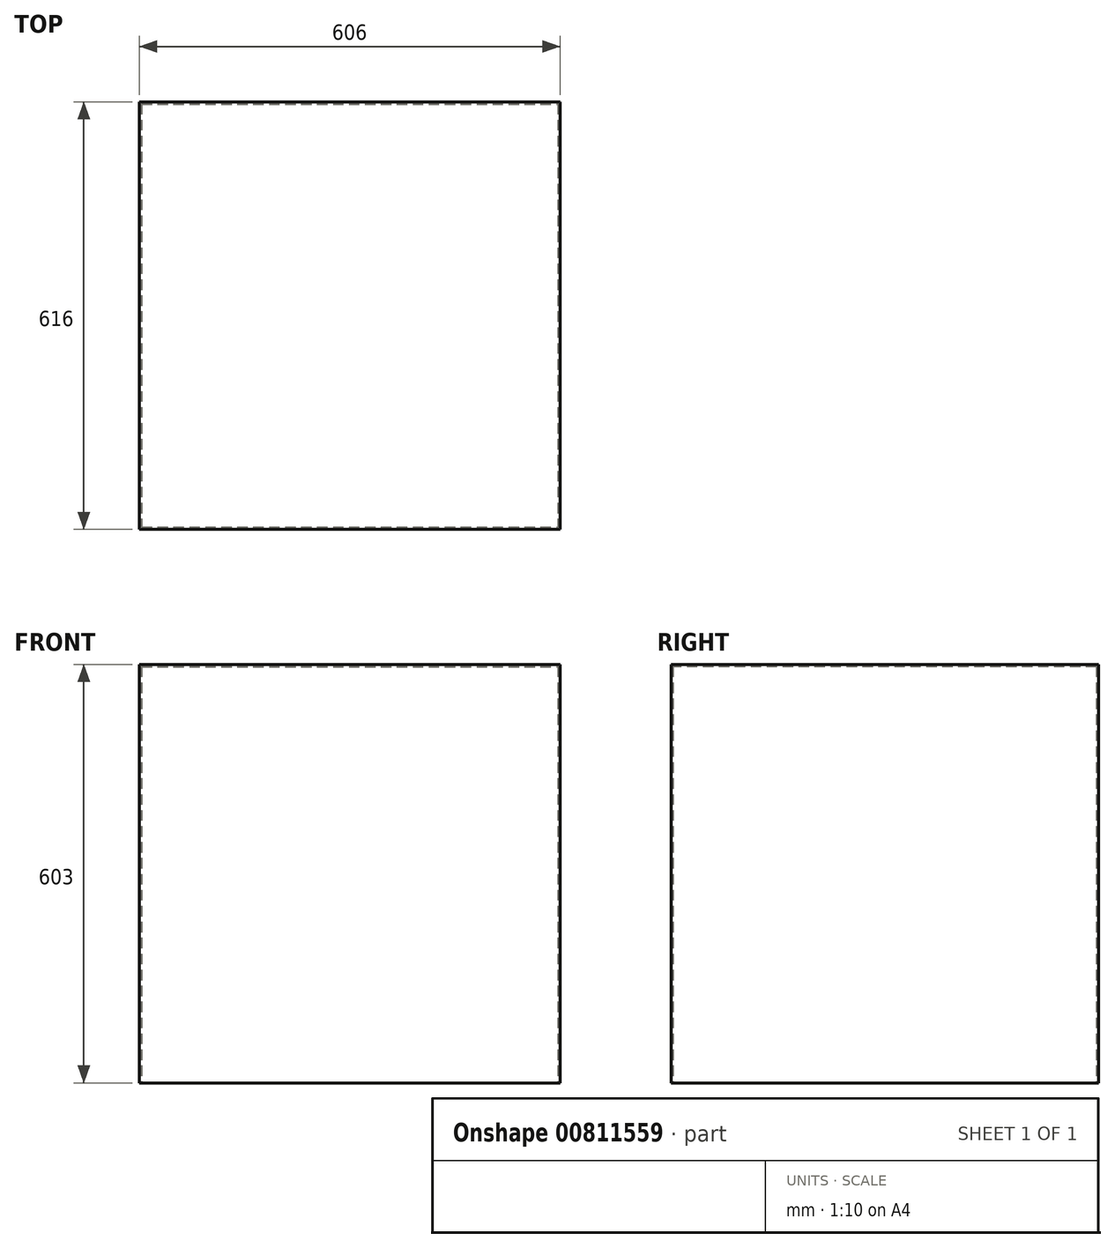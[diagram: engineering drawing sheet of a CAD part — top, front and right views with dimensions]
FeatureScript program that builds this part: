
annotation { "Feature Type Name" : "Feature", "Feature Type Description" : "" }
export const myFeature = defineFeature(function(context is Context, id is Id, definition is map)
    precondition{}
    {
        {
            var Q0;
            Q0=qCreatedBy(makeId("Top.planeOp"),FACE);
            var sketch = newSketch(context, id + "F0", { "sketchPlane" : qUnion([Q0])});
            skLineSegment(sketch, "E0.bottom", {"start": v(-301.78, 285.2) * mm, "end": v(304.22, 285.2) * mm});
            skLineSegment(sketch, "E0.top", {"start": v(-301.78, 282.2) * mm, "end": v(304.22, 282.2) * mm});
            skLineSegment(sketch, "E0.left", {"start": v(-301.78, 285.2) * mm, "end": v(-301.78, 282.2) * mm});
            skLineSegment(sketch, "E0.right", {"start": v(304.22, 285.2) * mm, "end": v(304.22, 282.2) * mm});
            skLineSegment(sketch, "E1.bottom", {"start": v(304.22, 282.2) * mm, "end": v(301.22, 282.2) * mm});
            skLineSegment(sketch, "E1.top", {"start": v(304.22, -327.8) * mm, "end": v(301.22, -327.8) * mm});
            skLineSegment(sketch, "E1.left", {"start": v(304.22, 282.2) * mm, "end": v(304.22, -327.8) * mm});
            skLineSegment(sketch, "E1.right", {"start": v(301.22, 282.2) * mm, "end": v(301.22, -327.8) * mm});
            skLineSegment(sketch, "E2.bottom", {"start": v(-301.78, 282.2) * mm, "end": v(-298.78, 282.2) * mm});
            skLineSegment(sketch, "E2.top", {"start": v(-301.78, -327.8) * mm, "end": v(-298.78, -327.8) * mm});
            skLineSegment(sketch, "E2.left", {"start": v(-301.78, 282.2) * mm, "end": v(-301.78, -327.8) * mm});
            skLineSegment(sketch, "E2.right", {"start": v(-298.78, 282.2) * mm, "end": v(-298.78, -327.8) * mm});
            skLineSegment(sketch, "E3.bottom", {"start": v(-301.78, -327.8) * mm, "end": v(304.22, -327.8) * mm});
            skLineSegment(sketch, "E3.top", {"start": v(-301.78, -330.8) * mm, "end": v(304.22, -330.8) * mm});
            skLineSegment(sketch, "E3.left", {"start": v(-301.78, -327.8) * mm, "end": v(-301.78, -330.8) * mm});
            skLineSegment(sketch, "E3.right", {"start": v(304.22, -327.8) * mm, "end": v(304.22, -330.8) * mm});
            skSolve(sketch);
        }
        {
            var Q0;
            Q0 = qSketchRegion(id + "F0", true);
            extrude(context, id + "F1", {"entities" : qUnion([Q0]), "depth" : 600 * mm, "offsetDistance" : 25 * mm});
        }
        {
            var Q0;
            Q0=makeQuery(id+"F1.opExtrude","CAP_FACE",FACE,{"disambiguationData":[OSD([sQuery(id+"F0.wireOp",EDGE,"E0.bottom"),sQuery(id+"F0.wireOp",EDGE,"E0.top"),sQuery(id+"F0.wireOp",EDGE,"E0.left"),sQuery(id+"F0.wireOp",EDGE,"E0.right"),sQuery(id+"F0.wireOp",EDGE,"E1.left"),sQuery(id+"F0.wireOp",EDGE,"E1.right"),sQuery(id+"F0.wireOp",EDGE,"E2.left"),sQuery(id+"F0.wireOp",EDGE,"E2.right"),sQuery(id+"F0.wireOp",EDGE,"E3.bottom"),sQuery(id+"F0.wireOp",EDGE,"E3.top"),sQuery(id+"F0.wireOp",EDGE,"E3.left"),sQuery(id+"F0.wireOp",EDGE,"E3.right")])],"isStart":false});
            var sketch = newSketch(context, id + "F2", { "sketchPlane" : qUnion([Q0])});
            skLineSegment(sketch, "E4.bottom", {"start": v(-301.78, 285.2) * mm, "end": v(304.22, 285.2) * mm});
            skLineSegment(sketch, "E4.top", {"start": v(-301.78, -330.8) * mm, "end": v(304.22, -330.8) * mm});
            skLineSegment(sketch, "E4.left", {"start": v(-301.78, 285.2) * mm, "end": v(-301.78, -330.8) * mm});
            skLineSegment(sketch, "E4.right", {"start": v(304.22, 285.2) * mm, "end": v(304.22, -330.8) * mm});
            skSolve(sketch);
        }
        {
            var Q0;
            Q0 = qSketchRegion(id + "F2", true);
            extrude(context, id + "F3", {"entities" : qUnion([Q0]), "operationType" : NewBodyOperationType.ADD, "depth" : 3 * mm, "offsetDistance" : 25 * mm});
        }
    });
